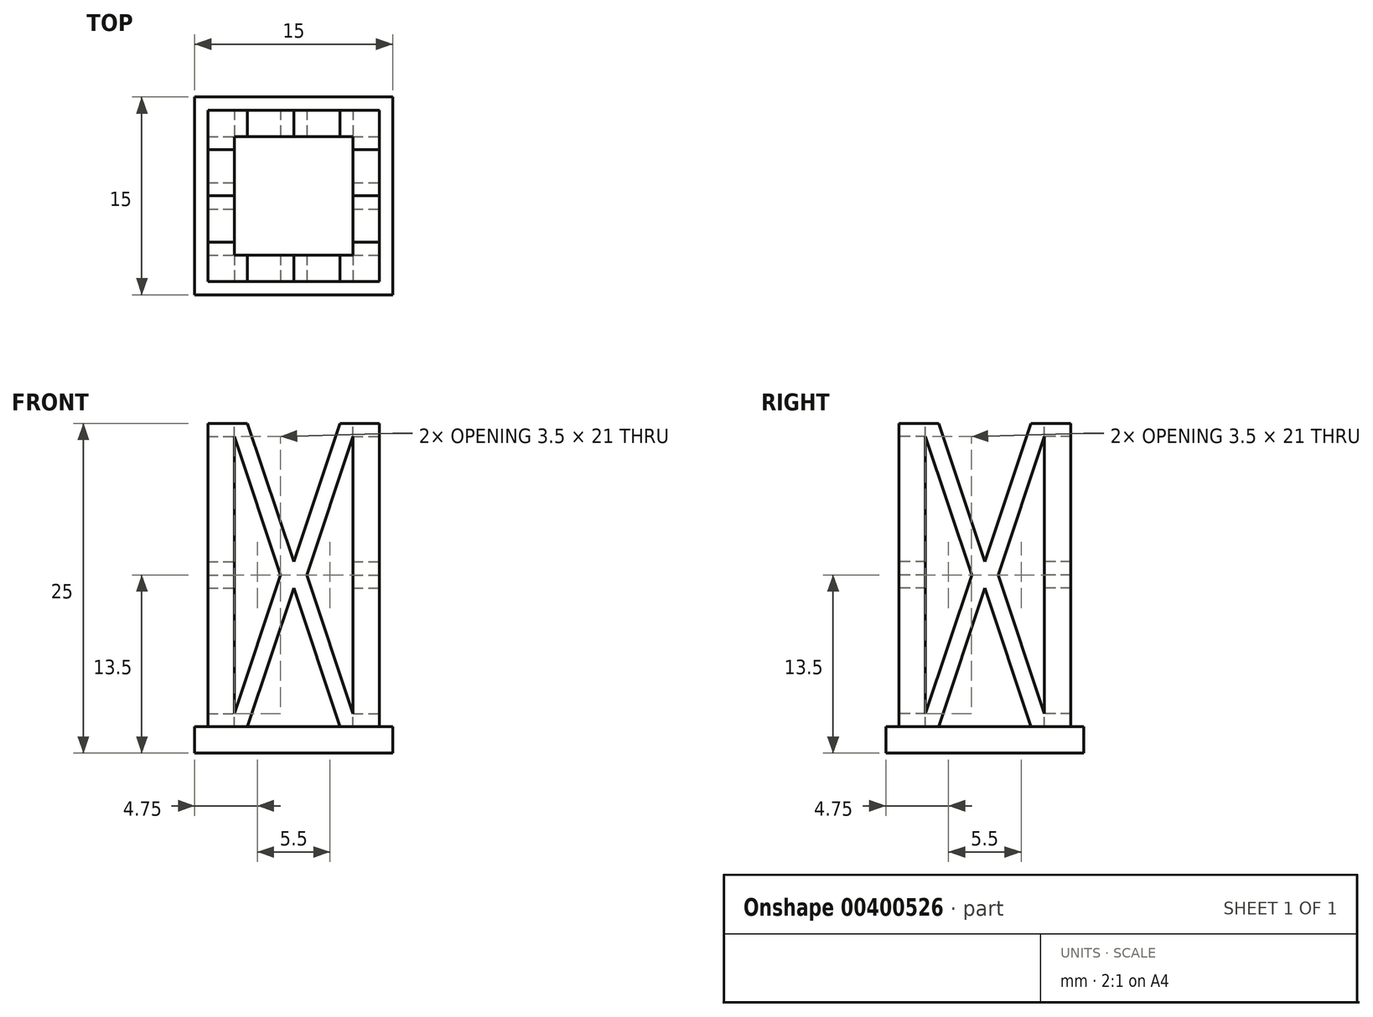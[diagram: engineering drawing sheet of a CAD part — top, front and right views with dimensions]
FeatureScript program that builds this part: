
annotation { "Feature Type Name" : "Feature", "Feature Type Description" : "" }
export const myFeature = defineFeature(function(context is Context, id is Id, definition is map)
    precondition{}
    {
        {
            var Q0;
            Q0=qCreatedBy(makeId("Top.planeOp"),FACE);
            var sketch = newSketch(context, id + "F0", { "sketchPlane" : qUnion([Q0])});
            skLineSegment(sketch, "E0.bottom", {"start": v(-7.5, 7.5) * mm, "end": v(7.5, 7.5) * mm});
            skLineSegment(sketch, "E0.top", {"start": v(-7.5, -7.5) * mm, "end": v(7.5, -7.5) * mm});
            skLineSegment(sketch, "E0.left", {"start": v(-7.5, 7.5) * mm, "end": v(-7.5, -7.5) * mm});
            skLineSegment(sketch, "E0.right", {"start": v(7.5, 7.5) * mm, "end": v(7.5, -7.5) * mm});
            skPoint(sketch, "E0.middle", {"position": v(0, 0) * mm});
            skSolve(sketch);
        }
        {
            var Q0;
            Q0 = qSketchRegion(id + "F0", true);
            extrude(context, id + "F1", {"entities" : qUnion([Q0]), "depth" : 25 * mm});
        }
        {
            var Q0;
            Q0=makeQuery(id+"F1.opExtrude","CAP_FACE",FACE,{"disambiguationData":[OSD([sQuery(id+"F0.wireOp",EDGE,"E0.bottom"),sQuery(id+"F0.wireOp",EDGE,"E0.top"),sQuery(id+"F0.wireOp",EDGE,"E0.left"),sQuery(id+"F0.wireOp",EDGE,"E0.right")])],"isStart":false});
            var sketch = newSketch(context, id + "F2", { "sketchPlane" : qUnion([Q0])});
            skLineSegment(sketch, "E1.bottom", {"start": v(-4.5, 4.5) * mm, "end": v(4.5, 4.5) * mm});
            skLineSegment(sketch, "E1.top", {"start": v(-4.5, -4.5) * mm, "end": v(4.5, -4.5) * mm});
            skLineSegment(sketch, "E1.left", {"start": v(-4.5, 4.5) * mm, "end": v(-4.5, -4.5) * mm});
            skLineSegment(sketch, "E1.right", {"start": v(4.5, 4.5) * mm, "end": v(4.5, -4.5) * mm});
            skPoint(sketch, "E1.middle", {"position": v(0, 0) * mm});
            skLineSegment(sketch, "E2.bottom", {"start": v(-7.5, 7.5) * mm, "end": v(7.5, 7.5) * mm});
            skLineSegment(sketch, "E2.top", {"start": v(-7.5, -7.5) * mm, "end": v(7.5, -7.5) * mm});
            skLineSegment(sketch, "E2.left", {"start": v(-7.5, 7.5) * mm, "end": v(-7.5, -7.5) * mm});
            skLineSegment(sketch, "E2.right", {"start": v(7.5, 7.5) * mm, "end": v(7.5, -7.5) * mm});
            skSolve(sketch);
        }
        {
            var Q0;
            Q0=makeQuery(id+"F2.imprint","IMPRINT",FACE,{"disambiguationData":[TD([[makeQuery(id+"F2.imprint","IMPRINT",EDGE,{"derivedFrom":sQuery(id+"F2.wireOp",EDGE,"E1.bottom")}),-1.0]])]});
            extrude(context, id + "F3", {"entities" : qUnion([Q0]), "operationType" : NewBodyOperationType.REMOVE, "oppositeDirection" : true, "depth" : 23 * mm});
        }
        {
            var Q0;
            Q0=makeQuery(id+"F1.opExtrude","SWEPT_FACE",FACE,{"disambiguationData":[OSD([sQuery(id+"F0.wireOp",EDGE,"E0.top")])]});
            var sketch = newSketch(context, id + "F4", { "sketchPlane" : qUnion([Q0])});
            skSolve(sketch);
        }
        {
            var Q0;
            {var subQ0=sQuery(id+"F0.wireOp",EDGE,"E0.top");Q0=makeQuery(id+"F4.imprint","IMPRINT",FACE,{"disambiguationData":[TD([[makeQuery(id+"F4.imprint","IMPRINT",EDGE,{"derivedFrom":makeQuery(id+"F1.opExtrude","CAP_EDGE",EDGE,{"disambiguationData":[OSD([subQ0])],"isStart":true})}),1.0]])]});}
            var sketch = newSketch(context, id + "F5", { "sketchPlane" : qUnion([Q0])});
            skLineSegment(sketch, "E3.bottom", {"start": v(-4.5, 25) * mm, "end": v(4.5, 25) * mm});
            skLineSegment(sketch, "E3.top", {"start": v(-4.5, 2) * mm, "end": v(4.5, 2) * mm});
            skLineSegment(sketch, "E3.left", {"start": v(-4.5, 25) * mm, "end": v(-4.5, 2) * mm});
            skLineSegment(sketch, "E3.right", {"start": v(4.5, 25) * mm, "end": v(4.5, 2) * mm});
            skLineSegment(sketch, "E4", {"start": v(-4.5, 13.5) * mm, "end": v(4.5, 13.5) * mm, "construction": true});
            skLineSegment(sketch, "E5", {"start": v(0, 25) * mm, "end": v(0, 2) * mm, "construction": true});
            skLineSegment(sketch, "E6", {"start": v(-3.5, 2) * mm, "end": v(0, 12.5) * mm});
            skLineSegment(sketch, "E7", {"start": v(-1, 13.5) * mm, "end": v(-4.5, 3) * mm});
            skPoint(sketch, "E8", {"position": v(0, 13.5) * mm});
            skLineSegment(sketch, "E9", {"start": v(0, 12.5) * mm, "end": v(3.5, 2) * mm});
            skLineSegment(sketch, "E10", {"start": v(-1, 13.5) * mm, "end": v(-4.5, 24) * mm});
            skLineSegment(sketch, "E11", {"start": v(0, 14.5) * mm, "end": v(-3.5, 25) * mm});
            skLineSegment(sketch, "E12", {"start": v(0, 14.5) * mm, "end": v(3.5, 25) * mm});
            skLineSegment(sketch, "E13", {"start": v(4.5, 24) * mm, "end": v(1, 13.5) * mm});
            skLineSegment(sketch, "E14", {"start": v(1, 13.5) * mm, "end": v(4.5, 3) * mm});
            skSolve(sketch);
        }
        {
            var Q0;
            {var subQ0=sQuery(id+"F5.wireOp",EDGE,"E11");Q0=makeQuery(id+"F5.imprint","IMPRINT",FACE,{"disambiguationData":[TD([[makeQuery(id+"F5.imprint","IMPRINT",EDGE,{"derivedFrom":subQ0}),-1.0]])]});}
            var Q1;
            {var subQ0=sQuery(id+"F5.wireOp",EDGE,"E6");Q1=makeQuery(id+"F5.imprint","IMPRINT",FACE,{"disambiguationData":[TD([[makeQuery(id+"F5.imprint","IMPRINT",EDGE,{"derivedFrom":subQ0}),-1.0]])]});}
            var Q2;
            {var subQ0=sQuery(id+"F5.wireOp",EDGE,"E7");Q2=makeQuery(id+"F5.imprint","IMPRINT",FACE,{"disambiguationData":[TD([[makeQuery(id+"F5.imprint","IMPRINT",EDGE,{"derivedFrom":subQ0}),-1.0]])]});}
            var Q3;
            {var subQ0=sQuery(id+"F5.wireOp",EDGE,"E13");Q3=makeQuery(id+"F5.imprint","IMPRINT",FACE,{"disambiguationData":[TD([[makeQuery(id+"F5.imprint","IMPRINT",EDGE,{"derivedFrom":subQ0}),1.0]])]});}
            extrude(context, id + "F6", {"entities" : qUnion([Q0, Q1, Q2, Q3]), "operationType" : NewBodyOperationType.REMOVE, "endBound" : BoundingType.THROUGH_ALL, "oppositeDirection" : true, "depth" : 25 * mm});
        }
        {
            var Q0;
            Q0=makeQuery(id+"F1.opExtrude","SWEPT_FACE",FACE,{"disambiguationData":[OSD([sQuery(id+"F0.wireOp",EDGE,"E0.right")])]});
            var sketch = newSketch(context, id + "F7", { "sketchPlane" : qUnion([Q0])});
            skLineSegment(sketch, "E15.bottom", {"start": v(-4.5, 25) * mm, "end": v(4.5, 25) * mm});
            skLineSegment(sketch, "E15.top", {"start": v(-4.5, 2) * mm, "end": v(4.5, 2) * mm});
            skLineSegment(sketch, "E15.left", {"start": v(-4.5, 25) * mm, "end": v(-4.5, 2) * mm});
            skLineSegment(sketch, "E15.right", {"start": v(4.5, 25) * mm, "end": v(4.5, 2) * mm});
            skLineSegment(sketch, "E16", {"start": v(-4.5, 13.5) * mm, "end": v(4.5, 13.5) * mm, "construction": true});
            skLineSegment(sketch, "E17", {"start": v(0, 25) * mm, "end": v(0, 2) * mm, "construction": true});
            skLineSegment(sketch, "E18", {"start": v(-3.5, 2) * mm, "end": v(0, 12.5) * mm});
            skLineSegment(sketch, "E19", {"start": v(-1, 13.5) * mm, "end": v(-4.5, 3) * mm});
            skPoint(sketch, "E20", {"position": v(0, 13.5) * mm});
            skLineSegment(sketch, "E21", {"start": v(0, 12.5) * mm, "end": v(3.5, 2) * mm});
            skLineSegment(sketch, "E22", {"start": v(-1, 13.5) * mm, "end": v(-4.5, 24) * mm});
            skLineSegment(sketch, "E23", {"start": v(0, 14.5) * mm, "end": v(-3.5, 25) * mm});
            skLineSegment(sketch, "E24", {"start": v(0, 14.5) * mm, "end": v(3.5, 25) * mm});
            skLineSegment(sketch, "E25", {"start": v(4.5, 24) * mm, "end": v(1, 13.5) * mm});
            skLineSegment(sketch, "E26", {"start": v(1, 13.5) * mm, "end": v(4.5, 3) * mm});
            skSolve(sketch);
        }
        {
            var Q0;
            {var subQ0=sQuery(id+"F7.wireOp",EDGE,"E23");Q0=makeQuery(id+"F7.imprint","IMPRINT",FACE,{"disambiguationData":[TD([[makeQuery(id+"F7.imprint","IMPRINT",EDGE,{"derivedFrom":subQ0}),-1.0]])]});}
            var Q1;
            {var subQ0=sQuery(id+"F7.wireOp",EDGE,"E18");Q1=makeQuery(id+"F7.imprint","IMPRINT",FACE,{"disambiguationData":[TD([[makeQuery(id+"F7.imprint","IMPRINT",EDGE,{"derivedFrom":subQ0}),-1.0]])]});}
            var Q2;
            {var subQ0=sQuery(id+"F7.wireOp",EDGE,"E25");Q2=makeQuery(id+"F7.imprint","IMPRINT",FACE,{"disambiguationData":[TD([[makeQuery(id+"F7.imprint","IMPRINT",EDGE,{"derivedFrom":subQ0}),1.0]])]});}
            var Q3;
            {var subQ0=sQuery(id+"F7.wireOp",EDGE,"E19");Q3=makeQuery(id+"F7.imprint","IMPRINT",FACE,{"disambiguationData":[TD([[makeQuery(id+"F7.imprint","IMPRINT",EDGE,{"derivedFrom":subQ0}),-1.0]])]});}
            extrude(context, id + "F8", {"entities" : qUnion([Q0, Q1, Q2, Q3]), "operationType" : NewBodyOperationType.REMOVE, "endBound" : BoundingType.THROUGH_ALL, "oppositeDirection" : true, "depth" : 25 * mm});
        }
        {
            var Q0;
            Q0=makeQuery(id+"F8.boolean.opBoolean","MERGE",FACE,{"derivedFrom":[makeQuery(id+"F6.boolean.opBoolean","MERGE",FACE,{"derivedFrom":[makeQuery(id+"F3.boolean.opBoolean","COPY",FACE,{"derivedFrom":makeQuery(id+"F3.opExtrude","CAP_FACE",FACE,{"disambiguationData":[OSD([sQuery(id+"F2.wireOp",EDGE,"E1.bottom"),sQuery(id+"F2.wireOp",EDGE,"E1.top"),sQuery(id+"F2.wireOp",EDGE,"E1.left"),sQuery(id+"F2.wireOp",EDGE,"E1.right")])],"isStart":false})}),makeQuery(id+"F6.opExtrude","SWEPT_FACE",FACE,{"disambiguationData":[OSD([sQuery(id+"F5.wireOp",EDGE,"E3.top")])]})]}),makeQuery(id+"F8.opExtrude","SWEPT_FACE",FACE,{"disambiguationData":[OSD([sQuery(id+"F7.wireOp",EDGE,"E15.top")])]})]});
            var sketch = newSketch(context, id + "F9", { "sketchPlane" : qUnion([Q0])});
            skLineSegment(sketch, "E27.bottom", {"start": v(-6.5, 6.5) * mm, "end": v(6.5, 6.5) * mm});
            skLineSegment(sketch, "E27.top", {"start": v(-6.5, -6.5) * mm, "end": v(6.5, -6.5) * mm});
            skLineSegment(sketch, "E27.left", {"start": v(-6.5, 6.5) * mm, "end": v(-6.5, -6.5) * mm});
            skLineSegment(sketch, "E27.right", {"start": v(6.5, 6.5) * mm, "end": v(6.5, -6.5) * mm});
            skPoint(sketch, "E27.middle", {"position": v(0, 0) * mm});
            skLineSegment(sketch, "E28.bottom", {"start": v(-7.5, 7.5) * mm, "end": v(7.5, 7.5) * mm});
            skLineSegment(sketch, "E28.top", {"start": v(-7.5, -7.5) * mm, "end": v(7.5, -7.5) * mm});
            skLineSegment(sketch, "E28.left", {"start": v(-7.5, 7.5) * mm, "end": v(-7.5, -7.5) * mm});
            skLineSegment(sketch, "E28.right", {"start": v(7.5, 7.5) * mm, "end": v(7.5, -7.5) * mm});
            skSolve(sketch);
        }
        {
            var Q0;
            Q0 = qSketchRegion(id + "F9", true);
            extrude(context, id + "F10", {"entities" : qUnion([Q0]), "operationType" : NewBodyOperationType.REMOVE, "depth" : 40.4 * mm});
        }
    });
